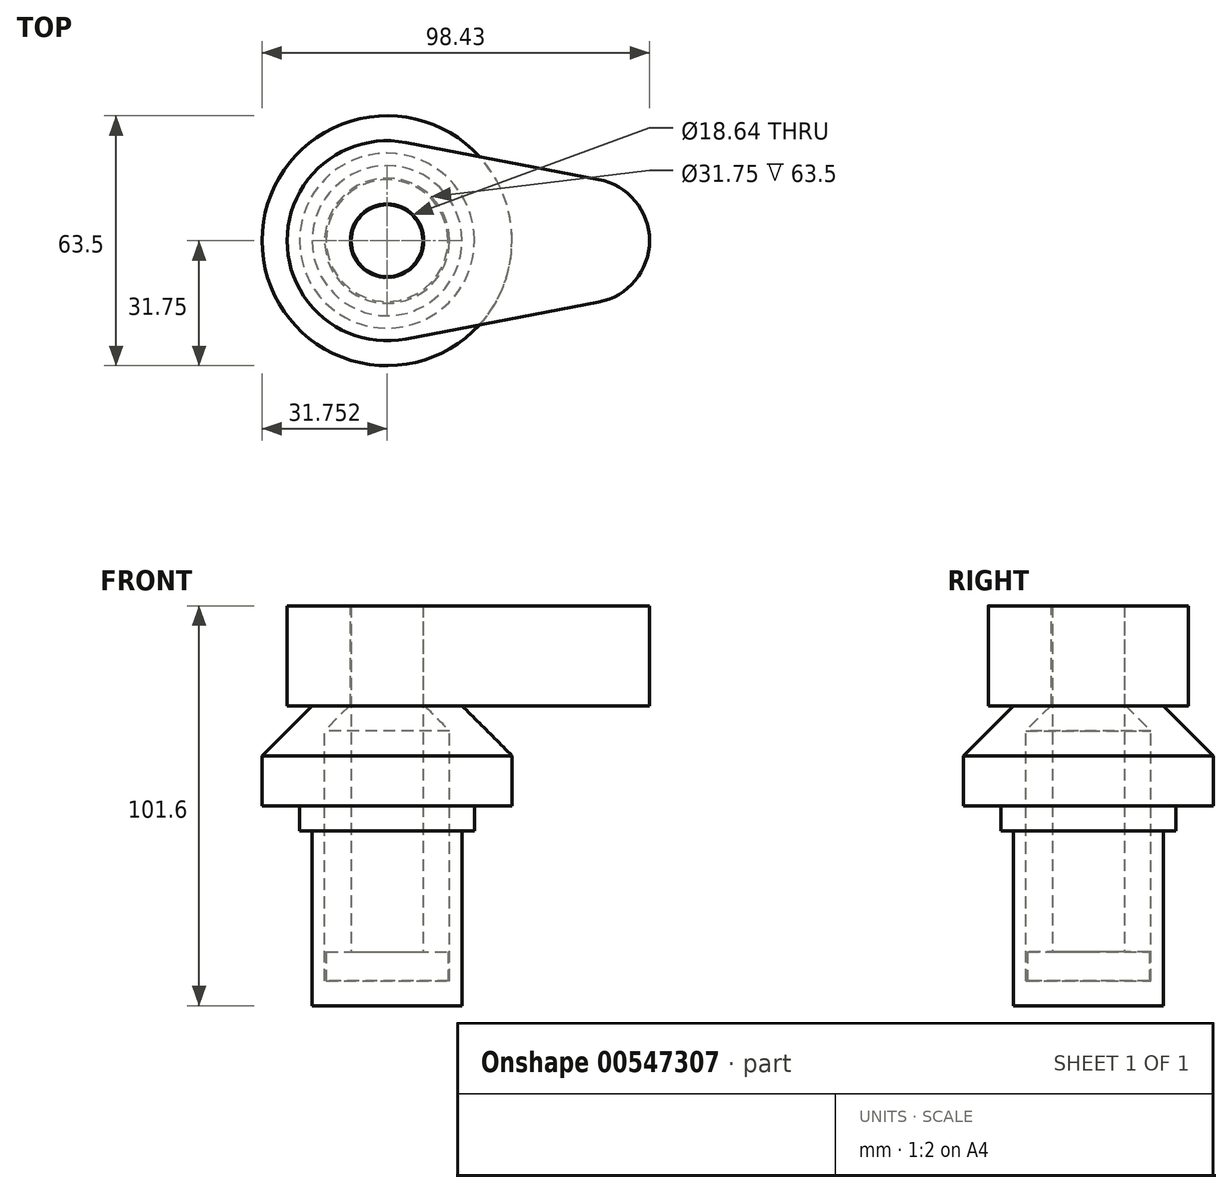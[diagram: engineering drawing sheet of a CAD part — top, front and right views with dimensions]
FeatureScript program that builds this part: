
annotation { "Feature Type Name" : "Feature", "Feature Type Description" : "" }
export const myFeature = defineFeature(function(context is Context, id is Id, definition is map)
    precondition{}
    {
        {
            var Q0;
            Q0=qCreatedBy(makeId("Front.planeOp"),FACE);
            var sketch = newSketch(context, id + "F0", { "sketchPlane" : qUnion([Q0])});
            skLineSegment(sketch, "E0", {"start": v(-16.37, 30.7) * mm, "end": v(2.68, 30.7) * mm});
            skLineSegment(sketch, "E1", {"start": v(2.68, 30.7) * mm, "end": v(15.38, 18) * mm});
            skLineSegment(sketch, "E2", {"start": v(15.38, 18) * mm, "end": v(15.38, 5.3) * mm});
            skLineSegment(sketch, "E3", {"start": v(15.38, 5.3) * mm, "end": v(5.86, 5.3) * mm});
            skLineSegment(sketch, "E4", {"start": v(5.86, 5.3) * mm, "end": v(5.86, -1.05) * mm});
            skLineSegment(sketch, "E5", {"start": v(5.86, -1.05) * mm, "end": v(2.68, -1.05) * mm});
            skLineSegment(sketch, "E6", {"start": v(2.68, -1.05) * mm, "end": v(2.68, -45.5) * mm});
            skLineSegment(sketch, "E7", {"start": v(2.68, -45.5) * mm, "end": v(-16.37, -45.5) * mm});
            skLineSegment(sketch, "E8", {"start": v(-16.37, -45.5) * mm, "end": v(-16.37, 30.7) * mm});
            skLineSegment(sketch, "E9", {"start": v(-16.37, -39.15) * mm, "end": v(-0.5, -39.15) * mm});
            skLineSegment(sketch, "E10", {"start": v(-0.5, -39.15) * mm, "end": v(-0.5, 24.35) * mm});
            skLineSegment(sketch, "E11", {"start": v(-0.5, 24.35) * mm, "end": v(-6.84, 30.7) * mm});
            skLineSegment(sketch, "E12", {"start": v(-16.37, 38.52) * mm, "end": v(-16.37, -68.78) * mm, "construction": true});
            skLineSegment(sketch, "E13", {"start": v(-16.37, 30.7) * mm, "end": v(-16.37, 56.1) * mm});
            skLineSegment(sketch, "E14", {"start": v(-16.37, 56.1) * mm, "end": v(-7.25, 56.1) * mm});
            skLineSegment(sketch, "E15", {"start": v(-7.25, 56.1) * mm, "end": v(-7.25, -31.77) * mm});
            skLineSegment(sketch, "E16", {"start": v(-7.25, -31.77) * mm, "end": v(-0.9, -31.77) * mm});
            skLineSegment(sketch, "E17", {"start": v(-0.9, -31.77) * mm, "end": v(-0.9, -39.15) * mm});
            skLineSegment(sketch, "E18", {"start": v(-0.9, -39.15) * mm, "end": v(-16.37, -39.15) * mm});
            skSolve(sketch);
        }
        {
            var Q0;
            {var subQ3=sQuery(id+"F0.wireOp",EDGE,"E1");Q0=makeQuery(id+"F0.imprint","IMPRINT",FACE,{"disambiguationData":[TD([[makeQuery(id+"F0.imprint","IMPRINT",EDGE,{"derivedFrom":subQ3}),-1.0]])]});}
            var Q1;
            Q1=sQuery(id+"F0.wireOp",EDGE,"E12");
            revolve(context, id + "F1", {"entities" : qUnion([Q0]), "axis" : qUnion([Q1]), "revolveType" : RevolveType.FULL});
        }
        {
            var Q0;
            {var subQ0=sQuery(id+"F0.wireOp",EDGE,"E13");Q0=makeQuery(id+"F0.imprint","IMPRINT",FACE,{"disambiguationData":[TD([[makeQuery(id+"F0.imprint","IMPRINT",EDGE,{"derivedFrom":subQ0}),-1.0]])]});}
            var Q1;
            {var subQ0=sQuery(id+"F0.wireOp",EDGE,"E16");Q1=makeQuery(id+"F0.imprint","IMPRINT",FACE,{"disambiguationData":[TD([[makeQuery(id+"F0.imprint","IMPRINT",EDGE,{"derivedFrom":subQ0}),-1.0]])]});}
            var Q2;
            Q2=sQuery(id+"F0.wireOp",EDGE,"E13");
            revolve(context, id + "F2", {"entities" : qUnion([Q0, Q1]), "axis" : qUnion([Q2]), "revolveType" : RevolveType.FULL});
        }
        {
            var Q0;
            Q0=makeQuery(id+"F2.opRevolve","SWEPT_FACE",FACE,{"disambiguationData":[OSD([sQuery(id+"F0.wireOp",EDGE,"E14")])]});
            var sketch = newSketch(context, id + "F3", { "sketchPlane" : qUnion([Q0])});
            skCircle(sketch, "E19", {"center": v(-16.37, 0) * mm, "radius": 25.4 * mm});
            skCircle(sketch, "E20", {"center": v(34.43, 0) * mm, "radius": 15.88 * mm});
            skLineSegment(sketch, "E21", {"start": v(-11.6, 24.95) * mm, "end": v(37.4, 15.6) * mm});
            skLineSegment(sketch, "E22", {"start": v(-11.6, -24.95) * mm, "end": v(37.4, -15.6) * mm});
            skCircle(sketch, "E23", {"center": v(-16.37, 0) * mm, "radius": 9.32 * mm});
            skSolve(sketch);
        }
        {
            var Q0;
            Q0=makeQuery(id+"F3.imprint","IMPRINT",FACE,{"disambiguationData":[TD([[makeQuery(id+"F3.imprint","IMPRINT",EDGE,{"derivedFrom":sQuery(id+"F3.wireOp",EDGE,"E23")}),-1.0]])]});
            var Q1;
            {var subQ0=sQuery(id+"F3.wireOp",EDGE,"E21");Q1=makeQuery(id+"F3.imprint","IMPRINT",FACE,{"disambiguationData":[TD([[makeQuery(id+"F3.imprint","IMPRINT",EDGE,{"derivedFrom":subQ0}),-1.0]])]});}
            var Q2;
            {var subQ0=sQuery(id+"F3.wireOp",EDGE,"E20");var subQ1=makeQuery(id+"F3.imprint","INTERSECT",VERTEX,{"derivedFrom":[subQ0,sQuery(id+"F3.wireOp",EDGE,"E21")]});Q2=makeQuery(id+"F3.imprint","IMPRINT",FACE,{"disambiguationData":[TD([[makeQuery(id+"F3.imprint","IMPRINT",EDGE,{"disambiguationData":[TD([[subQ1,-1.0]])],"derivedFrom":subQ0}),1.0]])]});}
            extrude(context, id + "F4", {"entities" : qUnion([Q0, Q1, Q2]), "oppositeDirection" : true, "depth" : 25.4 * mm, "offsetDistance" : 25.4 * mm});
        }
    });
